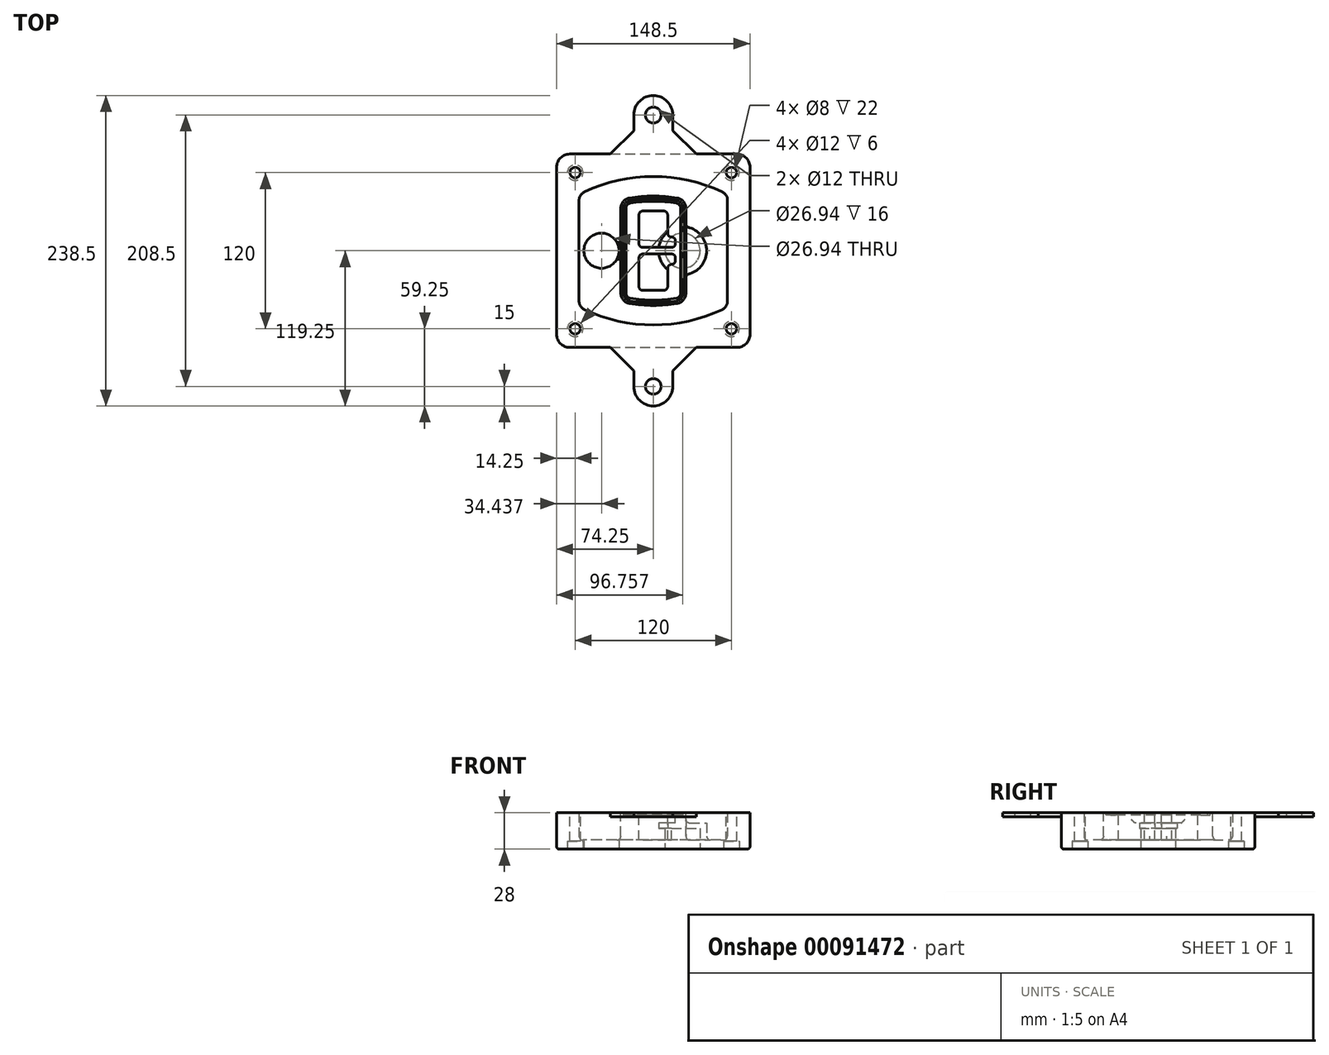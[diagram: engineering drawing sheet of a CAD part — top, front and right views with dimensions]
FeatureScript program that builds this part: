
annotation { "Feature Type Name" : "Feature", "Feature Type Description" : "" }
export const myFeature = defineFeature(function(context is Context, id is Id, definition is map)
    precondition{}
    {
        {
            var Q0;
            Q0=qCreatedBy(makeId("Top.planeOp"),FACE);
            var sketch = newSketch(context, id + "F0", { "sketchPlane" : qUnion([Q0])});
            skPoint(sketch, "E0.rect.middle", {"position": v(0, 0) * mm});
            skLineSegment(sketch, "E1.bottom", {"start": v(-64.25, -74.25) * mm, "end": v(64.25, -74.25) * mm});
            skLineSegment(sketch, "E1.top", {"start": v(-64.25, 74.25) * mm, "end": v(64.25, 74.25) * mm});
            skLineSegment(sketch, "E1.left", {"start": v(-74.25, -64.25) * mm, "end": v(-74.25, 64.25) * mm});
            skLineSegment(sketch, "E1.right", {"start": v(74.25, -64.25) * mm, "end": v(74.25, 64.25) * mm});
            skLineSegment(sketch, "E2", {"start": v(-74.25, 74.25) * mm, "end": v(74.25, -74.25) * mm, "construction": true});
            skLineSegment(sketch, "E3", {"start": v(74.25, 74.25) * mm, "end": v(-74.25, -74.25) * mm, "construction": true});
            skCircle(sketch, "E4", {"center": v(-60, 60) * mm, "radius": 4 * mm});
            skCircle(sketch, "E5", {"center": v(60, 60) * mm, "radius": 4 * mm});
            skCircle(sketch, "E6", {"center": v(60, -60) * mm, "radius": 4 * mm});
            skCircle(sketch, "E7", {"center": v(-60, -60) * mm, "radius": 4 * mm});
            skLineSegment(sketch, "E8", {"start": v(-60, 60) * mm, "end": v(60, 60) * mm, "construction": true});
            skLineSegment(sketch, "E9", {"start": v(60, 60) * mm, "end": v(60, -60) * mm, "construction": true});
            skLineSegment(sketch, "E10", {"start": v(60, -60) * mm, "end": v(-60, -60) * mm, "construction": true});
            skLineSegment(sketch, "E11", {"start": v(-60, -60) * mm, "end": v(-60, 60) * mm, "construction": true});
            skLineSegment(sketch, "E12", {"start": v(-60, 38.83) * mm, "end": v(-60, -38.83) * mm});
            skLineSegment(sketch, "E13", {"start": v(60, 38.83) * mm, "end": v(60, -38.83) * mm});
            skArc(sketch, "E14", {"start": v(54.26, 47.88) * mm, "mid": v(0, 60) * mm, "end": v(-54.26, 47.88) * mm});
            skArc(sketch, "E15", {"start": v(-54.26, -47.88) * mm, "mid": v(0, -60) * mm, "end": v(54.26, -47.88) * mm});
            skLineSegment(sketch, "E16", {"start": v(-60, 0) * mm, "end": v(60, 0) * mm, "construction": true});
            skPoint(sketch, "E17.visualSharp", {"position": v(-60, -45) * mm});
            skArc(sketch, "E17.filletArc", {"start": v(-60, -38.83) * mm, "mid": v(-58.44, -44.2) * mm, "end": v(-54.26, -47.88) * mm});
            skPoint(sketch, "E18.visualSharp", {"position": v(-60, 45) * mm});
            skArc(sketch, "E18.filletArc", {"start": v(-54.26, 47.88) * mm, "mid": v(-58.44, 44.2) * mm, "end": v(-60, 38.83) * mm});
            skPoint(sketch, "E19.visualSharp", {"position": v(60, 45) * mm});
            skArc(sketch, "E19.filletArc", {"start": v(60, 38.83) * mm, "mid": v(58.44, 44.2) * mm, "end": v(54.26, 47.88) * mm});
            skPoint(sketch, "E20.visualSharp", {"position": v(60, -45) * mm});
            skArc(sketch, "E20.filletArc", {"start": v(54.26, -47.88) * mm, "mid": v(58.44, -44.2) * mm, "end": v(60, -38.83) * mm});
            skPoint(sketch, "E21.visualSharp", {"position": v(-74.25, 74.25) * mm});
            skArc(sketch, "E21.filletArc", {"start": v(-64.25, 74.25) * mm, "mid": v(-71.32, 71.32) * mm, "end": v(-74.25, 64.25) * mm});
            skPoint(sketch, "E22.visualSharp", {"position": v(74.25, 74.25) * mm});
            skArc(sketch, "E22.filletArc", {"start": v(74.25, 64.25) * mm, "mid": v(71.32, 71.32) * mm, "end": v(64.25, 74.25) * mm});
            skPoint(sketch, "E23.visualSharp", {"position": v(74.25, -74.25) * mm});
            skArc(sketch, "E23.filletArc", {"start": v(64.25, -74.25) * mm, "mid": v(71.32, -71.32) * mm, "end": v(74.25, -64.25) * mm});
            skPoint(sketch, "E24.visualSharp", {"position": v(-74.25, -74.25) * mm});
            skArc(sketch, "E24.filletArc", {"start": v(-74.25, -64.25) * mm, "mid": v(-71.32, -71.32) * mm, "end": v(-64.25, -74.25) * mm});
            skArc(sketch, "E25.0", {"start": v(57, 38.83) * mm, "mid": v(55.9, 42.58) * mm, "end": v(52.98, 45.17) * mm});
            skLineSegment(sketch, "E25.1", {"start": v(57, 38.83) * mm, "end": v(57, -38.83) * mm});
            skArc(sketch, "E25.2", {"start": v(52.98, -45.17) * mm, "mid": v(55.9, -42.58) * mm, "end": v(57, -38.83) * mm});
            skArc(sketch, "E25.3", {"start": v(-52.98, -45.17) * mm, "mid": v(0, -57) * mm, "end": v(52.98, -45.17) * mm});
            skArc(sketch, "E25.4", {"start": v(-57, -38.83) * mm, "mid": v(-55.9, -42.58) * mm, "end": v(-52.98, -45.17) * mm});
            skArc(sketch, "E25.5", {"start": v(52.98, 45.17) * mm, "mid": v(0, 57) * mm, "end": v(-52.98, 45.17) * mm});
            skLineSegment(sketch, "E25.6", {"start": v(-57, 38.83) * mm, "end": v(-57, -38.83) * mm});
            skArc(sketch, "E25.7", {"start": v(-52.98, 45.17) * mm, "mid": v(-55.9, 42.58) * mm, "end": v(-57, 38.83) * mm});
            skArc(sketch, "E26.0", {"start": v(-55.96, 51.5) * mm, "mid": v(-61.82, 46.33) * mm, "end": v(-64, 38.83) * mm});
            skArc(sketch, "E26.1", {"start": v(55.96, 51.5) * mm, "mid": v(0, 64) * mm, "end": v(-55.96, 51.5) * mm});
            skArc(sketch, "E26.2", {"start": v(64, 38.83) * mm, "mid": v(61.82, 46.33) * mm, "end": v(55.96, 51.5) * mm});
            skLineSegment(sketch, "E26.3", {"start": v(64, 38.83) * mm, "end": v(64, -38.83) * mm});
            skArc(sketch, "E26.4", {"start": v(55.96, -51.5) * mm, "mid": v(61.82, -46.33) * mm, "end": v(64, -38.83) * mm});
            skLineSegment(sketch, "E26.5", {"start": v(-64, 38.83) * mm, "end": v(-64, -38.83) * mm});
            skArc(sketch, "E26.6", {"start": v(-55.96, -51.5) * mm, "mid": v(0, -64) * mm, "end": v(55.96, -51.5) * mm});
            skArc(sketch, "E26.7", {"start": v(-64, -38.83) * mm, "mid": v(-61.82, -46.33) * mm, "end": v(-55.96, -51.5) * mm});
            skSolve(sketch);
        }
        {
            var Q0;
            Q0=makeQuery(id+"F0.imprint","IMPRINT",FACE,{"disambiguationData":[TD([[makeQuery(id+"F0.imprint","IMPRINT",EDGE,{"derivedFrom":sQuery(id+"F0.wireOp",EDGE,"E1.bottom")}),1.0]])]});
            var Q1;
            Q1=makeQuery(id+"F0.imprint","IMPRINT",FACE,{"disambiguationData":[TD([[makeQuery(id+"F0.imprint","IMPRINT",EDGE,{"derivedFrom":sQuery(id+"F0.wireOp",EDGE,"E12")}),1.0]])]});
            var Q2;
            Q2=makeQuery(id+"F0.imprint","IMPRINT",FACE,{"disambiguationData":[TD([[makeQuery(id+"F0.imprint","IMPRINT",EDGE,{"derivedFrom":sQuery(id+"F0.wireOp",EDGE,"E25.0")}),1.0]])]});
            var Q3;
            Q3=makeQuery(id+"F0.imprint","IMPRINT",FACE,{"disambiguationData":[TD([[makeQuery(id+"F0.imprint","IMPRINT",EDGE,{"derivedFrom":sQuery(id+"F0.wireOp",EDGE,"E12")}),-1.0]])]});
            extrude(context, id + "F1", {"entities" : qUnion([Q0, Q1, Q2, Q3]), "oppositeDirection" : true, "depth" : 25 * mm});
        }
        {
            var Q0;
            Q0=makeQuery(id+"F0.imprint","IMPRINT",FACE,{"disambiguationData":[TD([[makeQuery(id+"F0.imprint","IMPRINT",EDGE,{"derivedFrom":sQuery(id+"F0.wireOp",EDGE,"E12")}),1.0]])]});
            extrude(context, id + "F2", {"entities" : qUnion([Q0]), "operationType" : NewBodyOperationType.ADD, "depth" : 3 * mm});
        }
        {
            var Q0;
            Q0=makeQuery(id+"F0.imprint","IMPRINT",FACE,{"disambiguationData":[TD([[makeQuery(id+"F0.imprint","IMPRINT",EDGE,{"derivedFrom":sQuery(id+"F0.wireOp",EDGE,"E25.0")}),1.0]])]});
            extrude(context, id + "F3", {"entities" : qUnion([Q0]), "operationType" : NewBodyOperationType.REMOVE, "oppositeDirection" : true, "depth" : 18 * mm});
        }
        {
            var Q0;
            Q0=makeQuery(id+"F2.opExtrude","CAP_FACE",FACE,{"disambiguationData":[OSD([sQuery(id+"F0.wireOp",EDGE,"E12"),sQuery(id+"F0.wireOp",EDGE,"E13"),sQuery(id+"F0.wireOp",EDGE,"E14"),sQuery(id+"F0.wireOp",EDGE,"E15"),sQuery(id+"F0.wireOp",EDGE,"E17.filletArc"),sQuery(id+"F0.wireOp",EDGE,"E18.filletArc"),sQuery(id+"F0.wireOp",EDGE,"E19.filletArc"),sQuery(id+"F0.wireOp",EDGE,"E20.filletArc"),sQuery(id+"F0.wireOp",EDGE,"E25.0"),sQuery(id+"F0.wireOp",EDGE,"E25.1"),sQuery(id+"F0.wireOp",EDGE,"E25.2"),sQuery(id+"F0.wireOp",EDGE,"E25.3"),sQuery(id+"F0.wireOp",EDGE,"E25.4"),sQuery(id+"F0.wireOp",EDGE,"E25.5"),sQuery(id+"F0.wireOp",EDGE,"E25.6"),sQuery(id+"F0.wireOp",EDGE,"E25.7")])],"isStart":false});
            var sketch = newSketch(context, id + "F4", { "sketchPlane" : qUnion([Q0])});
            skArc(sketch, "E27.0", {"start": v(-18.34, -40.45) * mm, "mid": v(0, -42) * mm, "end": v(18.34, -40.45) * mm});
            skArc(sketch, "E28.0", {"start": v(18.34, 40.45) * mm, "mid": v(0, 42) * mm, "end": v(-18.34, 40.45) * mm});
            skLineSegment(sketch, "E29", {"start": v(-25, 32.57) * mm, "end": v(-25, -32.57) * mm});
            skLineSegment(sketch, "E30", {"start": v(25, 32.57) * mm, "end": v(25, -32.57) * mm});
            skLineSegment(sketch, "E31", {"start": v(-25, 39.1) * mm, "end": v(25, 39.1) * mm, "construction": true});
            skLineSegment(sketch, "E32", {"start": v(-25, -39.1) * mm, "end": v(25, -39.1) * mm, "construction": true});
            skPoint(sketch, "E33.visualSharp", {"position": v(-25, 39.1) * mm});
            skArc(sketch, "E33.filletArc", {"start": v(-18.34, 40.45) * mm, "mid": v(-23.11, 37.73) * mm, "end": v(-25, 32.57) * mm});
            skPoint(sketch, "E34.visualSharp", {"position": v(25, 39.1) * mm});
            skArc(sketch, "E34.filletArc", {"start": v(25, 32.57) * mm, "mid": v(23.11, 37.73) * mm, "end": v(18.34, 40.45) * mm});
            skPoint(sketch, "E35.visualSharp", {"position": v(25, -39.1) * mm});
            skArc(sketch, "E35.filletArc", {"start": v(18.34, -40.45) * mm, "mid": v(23.11, -37.73) * mm, "end": v(25, -32.57) * mm});
            skPoint(sketch, "E36.visualSharp", {"position": v(-25, -39.1) * mm});
            skArc(sketch, "E36.filletArc", {"start": v(-25, -32.57) * mm, "mid": v(-23.11, -37.73) * mm, "end": v(-18.34, -40.45) * mm});
            skArc(sketch, "E37.0", {"start": v(52.98, 45.17) * mm, "mid": v(0, 57) * mm, "end": v(-52.98, 45.17) * mm});
            skArc(sketch, "E37.1", {"start": v(-52.98, 45.17) * mm, "mid": v(-55.9, 42.58) * mm, "end": v(-57, 38.83) * mm});
            skLineSegment(sketch, "E37.2", {"start": v(-57, 38.83) * mm, "end": v(-57, -38.83) * mm});
            skArc(sketch, "E37.3", {"start": v(-57, -38.83) * mm, "mid": v(-55.9, -42.58) * mm, "end": v(-52.98, -45.17) * mm});
            skArc(sketch, "E37.4", {"start": v(-52.98, -45.17) * mm, "mid": v(0, -57) * mm, "end": v(52.98, -45.17) * mm});
            skArc(sketch, "E37.5", {"start": v(52.98, -45.17) * mm, "mid": v(55.9, -42.58) * mm, "end": v(57, -38.83) * mm});
            skLineSegment(sketch, "E37.6", {"start": v(57, 38.83) * mm, "end": v(57, -38.83) * mm});
            skArc(sketch, "E37.7", {"start": v(57, 38.83) * mm, "mid": v(55.9, 42.58) * mm, "end": v(52.98, 45.17) * mm});
            skLineSegment(sketch, "E38.0", {"start": v(23, 32.57) * mm, "end": v(23, -32.57) * mm});
            skArc(sketch, "E38.1", {"start": v(18, -38.48) * mm, "mid": v(21.58, -36.44) * mm, "end": v(23, -32.57) * mm});
            skArc(sketch, "E38.2", {"start": v(-18, -38.48) * mm, "mid": v(0, -40) * mm, "end": v(18, -38.48) * mm});
            skArc(sketch, "E38.3", {"start": v(-23, -32.57) * mm, "mid": v(-21.58, -36.44) * mm, "end": v(-18, -38.48) * mm});
            skLineSegment(sketch, "E38.4", {"start": v(-23, 32.57) * mm, "end": v(-23, -32.57) * mm});
            skArc(sketch, "E38.5", {"start": v(23, 32.57) * mm, "mid": v(21.58, 36.44) * mm, "end": v(18, 38.48) * mm});
            skArc(sketch, "E38.6", {"start": v(-18, 38.48) * mm, "mid": v(-21.58, 36.44) * mm, "end": v(-23, 32.57) * mm});
            skArc(sketch, "E38.7", {"start": v(18, 38.48) * mm, "mid": v(0, 40) * mm, "end": v(-18, 38.48) * mm});
            skArc(sketch, "E39.0", {"start": v(21, 32.57) * mm, "mid": v(20.06, 35.15) * mm, "end": v(17.67, 36.5) * mm});
            skLineSegment(sketch, "E39.1", {"start": v(21, 32.57) * mm, "end": v(21, -32.57) * mm});
            skArc(sketch, "E39.2", {"start": v(17.67, -36.5) * mm, "mid": v(20.06, -35.15) * mm, "end": v(21, -32.57) * mm});
            skArc(sketch, "E39.3", {"start": v(-17.67, -36.5) * mm, "mid": v(0, -38) * mm, "end": v(17.67, -36.5) * mm});
            skArc(sketch, "E39.4", {"start": v(-21, -32.57) * mm, "mid": v(-20.06, -35.15) * mm, "end": v(-17.67, -36.5) * mm});
            skArc(sketch, "E39.5", {"start": v(17.67, 36.5) * mm, "mid": v(0, 38) * mm, "end": v(-17.67, 36.5) * mm});
            skLineSegment(sketch, "E39.6", {"start": v(-21, 32.57) * mm, "end": v(-21, -32.57) * mm});
            skArc(sketch, "E39.7", {"start": v(-17.67, 36.5) * mm, "mid": v(-20.06, 35.15) * mm, "end": v(-21, 32.57) * mm});
            skLineSegment(sketch, "E40", {"start": v(-25, 0) * mm, "end": v(25, 0) * mm, "construction": true});
            skLineSegment(sketch, "E41", {"start": v(-11, 5.5) * mm, "end": v(-11, 27.5) * mm});
            skLineSegment(sketch, "E42", {"start": v(-8, 30.5) * mm, "end": v(8, 30.5) * mm});
            skLineSegment(sketch, "E43", {"start": v(11, 27.5) * mm, "end": v(11, 13.5) * mm});
            skLineSegment(sketch, "E44", {"start": v(14, 10.5) * mm, "end": v(14, 10.5) * mm});
            skLineSegment(sketch, "E45", {"start": v(17, 7.5) * mm, "end": v(17, 5.5) * mm});
            skLineSegment(sketch, "E46", {"start": v(14, 2.5) * mm, "end": v(-8, 2.5) * mm});
            skPoint(sketch, "E47.visualSharp", {"position": v(-11, 30.5) * mm});
            skArc(sketch, "E47.filletArc", {"start": v(-8, 30.5) * mm, "mid": v(-10.12, 29.62) * mm, "end": v(-11, 27.5) * mm});
            skPoint(sketch, "E48.visualSharp", {"position": v(11, 30.5) * mm});
            skArc(sketch, "E48.filletArc", {"start": v(11, 27.5) * mm, "mid": v(10.12, 29.62) * mm, "end": v(8, 30.5) * mm});
            skPoint(sketch, "E49.visualSharp", {"position": v(11, 10.5) * mm});
            skArc(sketch, "E49.filletArc", {"start": v(11, 13.5) * mm, "mid": v(11.88, 11.38) * mm, "end": v(14, 10.5) * mm});
            skPoint(sketch, "E50.visualSharp", {"position": v(17, 10.5) * mm});
            skArc(sketch, "E50.filletArc", {"start": v(17, 7.5) * mm, "mid": v(16.12, 9.62) * mm, "end": v(14, 10.5) * mm});
            skPoint(sketch, "E51.visualSharp", {"position": v(17, 2.5) * mm});
            skArc(sketch, "E51.filletArc", {"start": v(14, 2.5) * mm, "mid": v(16.12, 3.38) * mm, "end": v(17, 5.5) * mm});
            skPoint(sketch, "E52.visualSharp", {"position": v(-11, 2.5) * mm});
            skArc(sketch, "E52.filletArc", {"start": v(-11, 5.5) * mm, "mid": v(-10.12, 3.38) * mm, "end": v(-8, 2.5) * mm});
            skLineSegment(sketch, "E53.0.MirrorCS", {"start": v(14, -2.5) * mm, "end": v(-8, -2.5) * mm});
            skArc(sketch, "E54.0.MirrorCS", {"start": v(-11, -5.5) * mm, "mid": v(-10.12, -3.38) * mm, "end": v(-8, -2.5) * mm});
            skLineSegment(sketch, "E55.0.MirrorCS", {"start": v(-11, -5.5) * mm, "end": v(-11, -27.5) * mm});
            skArc(sketch, "E56.0.MirrorCS", {"start": v(-8, -30.5) * mm, "mid": v(-10.12, -29.62) * mm, "end": v(-11, -27.5) * mm});
            skLineSegment(sketch, "E57.0.MirrorCS", {"start": v(-8, -30.5) * mm, "end": v(8, -30.5) * mm});
            skArc(sketch, "E58.0.MirrorCS", {"start": v(11, -27.5) * mm, "mid": v(10.12, -29.62) * mm, "end": v(8, -30.5) * mm});
            skLineSegment(sketch, "E59.0.MirrorCS", {"start": v(11, -27.5) * mm, "end": v(11, -13.5) * mm});
            skArc(sketch, "E60.0.MirrorCS", {"start": v(11, -13.5) * mm, "mid": v(11.88, -11.38) * mm, "end": v(14, -10.5) * mm});
            skArc(sketch, "E61.0.MirrorCS", {"start": v(17, -7.5) * mm, "mid": v(16.12, -9.62) * mm, "end": v(14, -10.5) * mm});
            skLineSegment(sketch, "E62.0.MirrorCS", {"start": v(17, -7.5) * mm, "end": v(17, -5.5) * mm});
            skArc(sketch, "E63.0.MirrorCS", {"start": v(14, -2.5) * mm, "mid": v(16.12, -3.38) * mm, "end": v(17, -5.5) * mm});
            skSolve(sketch);
        }
        {
            var Q0;
            Q0=makeQuery(id+"F4.imprint","IMPRINT",FACE,{"disambiguationData":[TD([[makeQuery(id+"F4.imprint","IMPRINT",EDGE,{"derivedFrom":sQuery(id+"F4.wireOp",EDGE,"E27.0")}),1.0]])]});
            var Q1;
            Q1=makeQuery(id+"F4.imprint","IMPRINT",FACE,{"disambiguationData":[TD([[makeQuery(id+"F4.imprint","IMPRINT",EDGE,{"derivedFrom":sQuery(id+"F4.wireOp",EDGE,"E38.0")}),-1.0]])]});
            var Q2;
            Q2=makeQuery(id+"F4.imprint","IMPRINT",FACE,{"disambiguationData":[TD([[makeQuery(id+"F4.imprint","IMPRINT",EDGE,{"derivedFrom":sQuery(id+"F4.wireOp",EDGE,"E39.0")}),1.0]])]});
            extrude(context, id + "F5", {"entities" : qUnion([Q0, Q1, Q2]), "operationType" : NewBodyOperationType.ADD, "endBound" : BoundingType.UP_TO_NEXT, "oppositeDirection" : true, "depth" : 25 * mm});
        }
        {
            var Q0;
            Q0=makeQuery(id+"F4.imprint","IMPRINT",FACE,{"disambiguationData":[TD([[makeQuery(id+"F4.imprint","IMPRINT",EDGE,{"derivedFrom":sQuery(id+"F4.wireOp",EDGE,"E38.0")}),-1.0]])]});
            extrude(context, id + "F6", {"entities" : qUnion([Q0]), "operationType" : NewBodyOperationType.REMOVE, "oppositeDirection" : true, "depth" : 2 * mm});
        }
        {
            var Q0;
            Q0=makeQuery(id+"F1.opExtrude","CAP_FACE",FACE,{"disambiguationData":[OSD([sQuery(id+"F0.wireOp",EDGE,"E1.bottom"),sQuery(id+"F0.wireOp",EDGE,"E1.top"),sQuery(id+"F0.wireOp",EDGE,"E1.left"),sQuery(id+"F0.wireOp",EDGE,"E1.right"),sQuery(id+"F0.wireOp",EDGE,"E4"),sQuery(id+"F0.wireOp",EDGE,"E5"),sQuery(id+"F0.wireOp",EDGE,"E6"),sQuery(id+"F0.wireOp",EDGE,"E7"),sQuery(id+"F0.wireOp",EDGE,"E21.filletArc"),sQuery(id+"F0.wireOp",EDGE,"E22.filletArc"),sQuery(id+"F0.wireOp",EDGE,"E23.filletArc"),sQuery(id+"F0.wireOp",EDGE,"E24.filletArc")])],"isStart":false});
            var sketch = newSketch(context, id + "F7", { "sketchPlane" : qUnion([Q0])});
            skCircle(sketch, "E64", {"center": v(22.5, 0) * mm, "radius": 13.47 * mm});
            skCircle(sketch, "E65", {"center": v(-39.81, 0) * mm, "radius": 13.47 * mm});
            skLineSegment(sketch, "E66", {"start": v(74.25, 0) * mm, "end": v(-74.25, 0) * mm});
            skCircle(sketch, "E67", {"center": v(22.5, 0) * mm, "radius": 18.47 * mm});
            skCircle(sketch, "E68", {"center": v(60, -60) * mm, "radius": 6 * mm});
            skCircle(sketch, "E69", {"center": v(-60, -60) * mm, "radius": 6 * mm});
            skCircle(sketch, "E70", {"center": v(-60, 60) * mm, "radius": 6 * mm});
            skCircle(sketch, "E71", {"center": v(60, 60) * mm, "radius": 6 * mm});
            skSolve(sketch);
        }
        {
            var Q0;
            {var subQ1=sQuery(id+"F7.wireOp",EDGE,"E66");var subQ4=sQuery(id+"F7.wireOp",EDGE,"E64");var subQ6=makeQuery(id+"F7.imprint","INTERSECT",VERTEX,{"disambiguationData":[OD(0.0)],"derivedFrom":[subQ4,subQ1]});Q0=makeQuery(id+"F7.imprint","IMPRINT",FACE,{"disambiguationData":[TD([[makeQuery(id+"F7.imprint","IMPRINT",EDGE,{"disambiguationData":[TD([[subQ6,-1.0]])],"derivedFrom":subQ4}),-1.0]])]});}
            var Q1;
            {var subQ0=sQuery(id+"F7.wireOp",EDGE,"E66");var subQ1=sQuery(id+"F7.wireOp",EDGE,"E64");var subQ3=makeQuery(id+"F7.imprint","INTERSECT",VERTEX,{"disambiguationData":[OD(0.0)],"derivedFrom":[subQ1,subQ0]});Q1=makeQuery(id+"F7.imprint","IMPRINT",FACE,{"disambiguationData":[TD([[makeQuery(id+"F7.imprint","IMPRINT",EDGE,{"disambiguationData":[TD([[subQ3,-1.0]])],"derivedFrom":subQ1}),1.0]])]});}
            var Q2;
            {var subQ0=sQuery(id+"F7.wireOp",EDGE,"E66");var subQ1=sQuery(id+"F7.wireOp",EDGE,"E64");var subQ3=makeQuery(id+"F7.imprint","INTERSECT",VERTEX,{"disambiguationData":[OD(0.0)],"derivedFrom":[subQ1,subQ0]});Q2=makeQuery(id+"F7.imprint","IMPRINT",FACE,{"disambiguationData":[TD([[makeQuery(id+"F7.imprint","IMPRINT",EDGE,{"disambiguationData":[TD([[subQ3,1.0]])],"derivedFrom":subQ1}),1.0]])]});}
            var Q3;
            {var subQ1=sQuery(id+"F7.wireOp",EDGE,"E66");var subQ4=sQuery(id+"F7.wireOp",EDGE,"E64");var subQ6=makeQuery(id+"F7.imprint","INTERSECT",VERTEX,{"disambiguationData":[OD(0.0)],"derivedFrom":[subQ4,subQ1]});Q3=makeQuery(id+"F7.imprint","IMPRINT",FACE,{"disambiguationData":[TD([[makeQuery(id+"F7.imprint","IMPRINT",EDGE,{"disambiguationData":[TD([[subQ6,1.0]])],"derivedFrom":subQ4}),-1.0]])]});}
            extrude(context, id + "F8", {"entities" : qUnion([Q0, Q1, Q2, Q3]), "operationType" : NewBodyOperationType.ADD, "oppositeDirection" : true, "depth" : 20 * mm});
        }
        {
            var Q0;
            {var subQ0=sQuery(id+"F7.wireOp",EDGE,"E66");var subQ1=sQuery(id+"F7.wireOp",EDGE,"E64");var subQ3=makeQuery(id+"F7.imprint","INTERSECT",VERTEX,{"disambiguationData":[OD(0.0)],"derivedFrom":[subQ1,subQ0]});Q0=makeQuery(id+"F7.imprint","IMPRINT",FACE,{"disambiguationData":[TD([[makeQuery(id+"F7.imprint","IMPRINT",EDGE,{"disambiguationData":[TD([[subQ3,-1.0]])],"derivedFrom":subQ1}),1.0]])]});}
            var Q1;
            {var subQ0=sQuery(id+"F7.wireOp",EDGE,"E66");var subQ1=sQuery(id+"F7.wireOp",EDGE,"E64");var subQ3=makeQuery(id+"F7.imprint","INTERSECT",VERTEX,{"disambiguationData":[OD(0.0)],"derivedFrom":[subQ1,subQ0]});Q1=makeQuery(id+"F7.imprint","IMPRINT",FACE,{"disambiguationData":[TD([[makeQuery(id+"F7.imprint","IMPRINT",EDGE,{"disambiguationData":[TD([[subQ3,1.0]])],"derivedFrom":subQ1}),1.0]])]});}
            extrude(context, id + "F9", {"entities" : qUnion([Q0, Q1]), "operationType" : NewBodyOperationType.REMOVE, "oppositeDirection" : true, "depth" : 16 * mm});
        }
        {
            var Q0;
            {var subQ0=sQuery(id+"F7.wireOp",EDGE,"E66");var subQ1=sQuery(id+"F7.wireOp",EDGE,"E65");var subQ3=makeQuery(id+"F7.imprint","INTERSECT",VERTEX,{"disambiguationData":[OD(0.0)],"derivedFrom":[subQ1,subQ0]});Q0=makeQuery(id+"F7.imprint","IMPRINT",FACE,{"disambiguationData":[TD([[makeQuery(id+"F7.imprint","IMPRINT",EDGE,{"disambiguationData":[TD([[subQ3,-1.0]])],"derivedFrom":subQ1}),1.0]])]});}
            var Q1;
            {var subQ0=sQuery(id+"F7.wireOp",EDGE,"E66");var subQ1=sQuery(id+"F7.wireOp",EDGE,"E65");var subQ3=makeQuery(id+"F7.imprint","INTERSECT",VERTEX,{"disambiguationData":[OD(0.0)],"derivedFrom":[subQ1,subQ0]});Q1=makeQuery(id+"F7.imprint","IMPRINT",FACE,{"disambiguationData":[TD([[makeQuery(id+"F7.imprint","IMPRINT",EDGE,{"disambiguationData":[TD([[subQ3,1.0]])],"derivedFrom":subQ1}),1.0]])]});}
            extrude(context, id + "F10", {"entities" : qUnion([Q0, Q1]), "operationType" : NewBodyOperationType.REMOVE, "oppositeDirection" : true, "depth" : 25 * mm});
        }
        {
            var Q0;
            Q0=makeQuery(id+"F7.imprint","IMPRINT",FACE,{"disambiguationData":[TD([[makeQuery(id+"F7.imprint","IMPRINT",EDGE,{"derivedFrom":sQuery(id+"F7.wireOp",EDGE,"E68")}),1.0]])]});
            var Q1;
            Q1=makeQuery(id+"F7.imprint","IMPRINT",FACE,{"disambiguationData":[TD([[makeQuery(id+"F7.imprint","IMPRINT",EDGE,{"derivedFrom":makeQuery(id+"F1.opExtrude","CAP_EDGE",EDGE,{"disambiguationData":[OSD([sQuery(id+"F0.wireOp",EDGE,"E5")])],"isStart":false})}),-1.0]])]});
            var Q2;
            Q2=makeQuery(id+"F7.imprint","IMPRINT",FACE,{"disambiguationData":[TD([[makeQuery(id+"F7.imprint","IMPRINT",EDGE,{"derivedFrom":sQuery(id+"F7.wireOp",EDGE,"E69")}),1.0]])]});
            var Q3;
            Q3=makeQuery(id+"F7.imprint","IMPRINT",FACE,{"disambiguationData":[TD([[makeQuery(id+"F7.imprint","IMPRINT",EDGE,{"derivedFrom":makeQuery(id+"F1.opExtrude","CAP_EDGE",EDGE,{"disambiguationData":[OSD([sQuery(id+"F0.wireOp",EDGE,"E4")])],"isStart":false})}),-1.0]])]});
            var Q4;
            Q4=makeQuery(id+"F7.imprint","IMPRINT",FACE,{"disambiguationData":[TD([[makeQuery(id+"F7.imprint","IMPRINT",EDGE,{"derivedFrom":sQuery(id+"F7.wireOp",EDGE,"E70")}),1.0]])]});
            var Q5;
            Q5=makeQuery(id+"F7.imprint","IMPRINT",FACE,{"disambiguationData":[TD([[makeQuery(id+"F7.imprint","IMPRINT",EDGE,{"derivedFrom":makeQuery(id+"F1.opExtrude","CAP_EDGE",EDGE,{"disambiguationData":[OSD([sQuery(id+"F0.wireOp",EDGE,"E7")])],"isStart":false})}),-1.0]])]});
            var Q6;
            Q6=makeQuery(id+"F7.imprint","IMPRINT",FACE,{"disambiguationData":[TD([[makeQuery(id+"F7.imprint","IMPRINT",EDGE,{"derivedFrom":sQuery(id+"F7.wireOp",EDGE,"E71")}),1.0]])]});
            var Q7;
            Q7=makeQuery(id+"F7.imprint","IMPRINT",FACE,{"disambiguationData":[TD([[makeQuery(id+"F7.imprint","IMPRINT",EDGE,{"derivedFrom":makeQuery(id+"F1.opExtrude","CAP_EDGE",EDGE,{"disambiguationData":[OSD([sQuery(id+"F0.wireOp",EDGE,"E6")])],"isStart":false})}),-1.0]])]});
            extrude(context, id + "F11", {"entities" : qUnion([Q0, Q1, Q2, Q3, Q4, Q5, Q6, Q7]), "operationType" : NewBodyOperationType.REMOVE, "oppositeDirection" : true, "depth" : 6 * mm});
        }
        {
            var Q0;
            Q0=makeQuery(id+"F9.boolean.opBoolean","COPY",FACE,{"derivedFrom":makeQuery(id+"F9.opExtrude","CAP_FACE",FACE,{"disambiguationData":[OSD([sQuery(id+"F7.wireOp",EDGE,"E64")])],"isStart":false})});
            var sketch = newSketch(context, id + "F12", { "sketchPlane" : qUnion([Q0])});
            skArc(sketch, "E72.0", {"start": v(11, 14.45) * mm, "mid": v(6.45, 9.13) * mm, "end": v(4.2, 2.5) * mm});
            skArc(sketch, "E72.1", {"start": v(4.2, -2.5) * mm, "mid": v(6.45, -9.13) * mm, "end": v(11, -14.45) * mm});
            skLineSegment(sketch, "E73", {"start": v(4.2, -2.5) * mm, "end": v(14, -2.5) * mm});
            skLineSegment(sketch, "E74.0", {"start": v(14, 2.5) * mm, "end": v(4.2, 2.5) * mm});
            skArc(sketch, "E74.1", {"start": v(14, 2.5) * mm, "mid": v(16.12, 3.38) * mm, "end": v(17, 5.5) * mm});
            skLineSegment(sketch, "E74.2", {"start": v(17, 7.5) * mm, "end": v(17, 5.5) * mm});
            skArc(sketch, "E74.3", {"start": v(17, 7.5) * mm, "mid": v(16.12, 9.62) * mm, "end": v(14, 10.5) * mm});
            skArc(sketch, "E74.4", {"start": v(11, 13.5) * mm, "mid": v(11.88, 11.38) * mm, "end": v(14, 10.5) * mm});
            skLineSegment(sketch, "E74.5", {"start": v(11, 14.45) * mm, "end": v(11, 13.5) * mm});
            skLineSegment(sketch, "E74.7", {"start": v(14, -2.5) * mm, "end": v(4.2, -2.5) * mm});
            skArc(sketch, "E74.8", {"start": v(14, -2.5) * mm, "mid": v(16.12, -3.38) * mm, "end": v(17, -5.5) * mm});
            skLineSegment(sketch, "E74.9", {"start": v(17, -7.5) * mm, "end": v(17, -5.5) * mm});
            skArc(sketch, "E74.10", {"start": v(17, -7.5) * mm, "mid": v(16.12, -9.62) * mm, "end": v(14, -10.5) * mm});
            skArc(sketch, "E74.11", {"start": v(11, -13.5) * mm, "mid": v(11.88, -11.38) * mm, "end": v(14, -10.5) * mm});
            skLineSegment(sketch, "E74.12", {"start": v(11, -14.45) * mm, "end": v(11, -13.5) * mm});
            skPoint(sketch, "E75.orphan", {"position": v(11, -27.5) * mm});
            skPoint(sketch, "E76.orphan", {"position": v(-8, -2.5) * mm});
            skPoint(sketch, "E77.orphan", {"position": v(-8, 2.5) * mm});
            skPoint(sketch, "E78.orphan", {"position": v(11, 27.5) * mm});
            skSolve(sketch);
        }
        {
            var Q0;
            {var subQ7=sQuery(id+"F12.wireOp",EDGE,"E72.0");var subQ14=sQuery(id+"F12.wireOp",EDGE,"E72.1");var subQ16=sQuery(id+"F12.wireOp",EDGE,"E74.1");var subQ18=sQuery(id+"F12.wireOp",EDGE,"E74.8");Q0=qUnion([makeQuery(id+"F12.imprint","IMPRINT",FACE,{"disambiguationData":[TD([[makeQuery(id+"F12.imprint","IMPRINT",EDGE,{"derivedFrom":subQ7}),1.0]])]}),makeQuery(id+"F12.imprint","IMPRINT",FACE,{"disambiguationData":[TD([[makeQuery(id+"F12.imprint","IMPRINT",EDGE,{"derivedFrom":subQ14}),1.0]])]}),makeQuery(id+"F12.imprint","IMPRINT",FACE,{"disambiguationData":[TD([[makeQuery(id+"F12.imprint","IMPRINT",EDGE,{"derivedFrom":subQ16}),1.0]])]}),makeQuery(id+"F12.imprint","IMPRINT",FACE,{"disambiguationData":[TD([[makeQuery(id+"F12.imprint","IMPRINT",EDGE,{"derivedFrom":subQ18}),-1.0]])]})]);}
            var Q1;
            Q1=makeQuery(id+"F5.boolean.opBoolean","SPLIT",FACE,{"disambiguationData":[TD([makeQuery(id+"F5.opExtrude","SWEPT_FACE",FACE,{"disambiguationData":[OSD([sQuery(id+"F4.wireOp",EDGE,"E41")])]})])],"derivedFrom":makeQuery(id+"F3.boolean.opBoolean","COPY",FACE,{"derivedFrom":makeQuery(id+"F3.opExtrude","CAP_FACE",FACE,{"disambiguationData":[OSD([sQuery(id+"F0.wireOp",EDGE,"E25.0"),sQuery(id+"F0.wireOp",EDGE,"E25.1"),sQuery(id+"F0.wireOp",EDGE,"E25.2"),sQuery(id+"F0.wireOp",EDGE,"E25.3"),sQuery(id+"F0.wireOp",EDGE,"E25.4"),sQuery(id+"F0.wireOp",EDGE,"E25.5"),sQuery(id+"F0.wireOp",EDGE,"E25.6"),sQuery(id+"F0.wireOp",EDGE,"E25.7")])],"isStart":false})})});
            extrude(context, id + "F13", {"entities" : qUnion([Q0]), "operationType" : NewBodyOperationType.REMOVE, "endBound" : BoundingType.UP_TO_SURFACE, "endBoundEntityFace" : qUnion([Q1]), "depth" : 25 * mm});
        }
        {
            var Q0;
            Q0=makeQuery(id+"F3.boolean.opBoolean","COPY",EDGE,{"derivedFrom":makeQuery(id+"F3.opExtrude","CAP_EDGE",EDGE,{"disambiguationData":[OSD([sQuery(id+"F0.wireOp",EDGE,"E25.6")])],"isStart":false})});
            var Q1;
            Q1=makeQuery(id+"F8.boolean.opBoolean","INTERSECT",EDGE,{"derivedFrom":[makeQuery(id+"F5.opExtrude","SWEPT_FACE",FACE,{"disambiguationData":[OSD([sQuery(id+"F4.wireOp",EDGE,"E30")])]}),makeQuery(id+"F8.opExtrude","CAP_FACE",FACE,{"disambiguationData":[OSD([sQuery(id+"F7.wireOp",EDGE,"E67")])],"isStart":false})]});
            var Q2;
            Q2=makeQuery(id+"F8.boolean.opBoolean","INTERSECT",EDGE,{"disambiguationData":[OD(1.0)],"derivedFrom":[makeQuery(id+"F5.opExtrude","SWEPT_FACE",FACE,{"disambiguationData":[OSD([sQuery(id+"F4.wireOp",EDGE,"E30")])]}),makeQuery(id+"F8.opExtrude","SWEPT_FACE",FACE,{"disambiguationData":[OSD([sQuery(id+"F7.wireOp",EDGE,"E67")])]})]});
            var Q3;
            {var subQ0=sQuery(id+"F4.wireOp",EDGE,"E30");Q3=makeQuery(id+"F8.boolean.opBoolean","SPLIT",EDGE,{"disambiguationData":[TD([makeQuery(id+"F5.opExtrude","SWEPT_FACE",FACE,{"disambiguationData":[OSD([sQuery(id+"F4.wireOp",EDGE,"E35.filletArc")])]})])],"derivedFrom":makeQuery(id+"F5.opExtrude","CAP_EDGE",EDGE,{"disambiguationData":[OSD([subQ0])],"isStart":false})});}
            var Q4;
            {var subQ0=sQuery(id+"F0.wireOp",EDGE,"E25.7");var subQ1=sQuery(id+"F0.wireOp",EDGE,"E25.1");var subQ2=sQuery(id+"F0.wireOp",EDGE,"E25.6");var subQ3=sQuery(id+"F0.wireOp",EDGE,"E25.5");var subQ4=sQuery(id+"F0.wireOp",EDGE,"E25.4");var subQ5=sQuery(id+"F0.wireOp",EDGE,"E25.0");var subQ6=sQuery(id+"F0.wireOp",EDGE,"E25.2");var subQ7=sQuery(id+"F0.wireOp",EDGE,"E25.3");Q4=makeQuery(id+"F8.boolean.opBoolean","INTERSECT",EDGE,{"derivedFrom":[makeQuery(id+"F5.boolean.opBoolean","SPLIT",FACE,{"disambiguationData":[TD([makeQuery(id+"F2.opExtrude","SWEPT_FACE",FACE,{"disambiguationData":[OSD([subQ5])]})])],"derivedFrom":makeQuery(id+"F3.boolean.opBoolean","COPY",FACE,{"derivedFrom":makeQuery(id+"F3.opExtrude","CAP_FACE",FACE,{"disambiguationData":[OSD([subQ5,subQ1,subQ6,subQ7,subQ4,subQ3,subQ2,subQ0])],"isStart":false})})}),makeQuery(id+"F8.opExtrude","SWEPT_FACE",FACE,{"disambiguationData":[OSD([sQuery(id+"F7.wireOp",EDGE,"E67")])]})]});}
            var Q5;
            Q5=makeQuery(id+"F8.boolean.opBoolean","INTERSECT",EDGE,{"disambiguationData":[OD(0.0)],"derivedFrom":[makeQuery(id+"F5.opExtrude","SWEPT_FACE",FACE,{"disambiguationData":[OSD([sQuery(id+"F4.wireOp",EDGE,"E30")])]}),makeQuery(id+"F8.opExtrude","SWEPT_FACE",FACE,{"disambiguationData":[OSD([sQuery(id+"F7.wireOp",EDGE,"E67")])]})]});
            fillet(context, id + "F14", {"entities" : qUnion([Q0, Q1, Q2, Q3, Q4, Q5]), "radius" : 3 * mm, "tangentPropagation" : true, "allowEdgeOverflow" : false});
        }
        {
            var Q0;
            Q0=makeQuery(id+"F1.opExtrude","CAP_EDGE",EDGE,{"disambiguationData":[OSD([sQuery(id+"F0.wireOp",EDGE,"E1.bottom")])],"isStart":false});
            fillet(context, id + "F15", {"entities" : qUnion([Q0]), "radius" : 2 * mm, "tangentPropagation" : true, "allowEdgeOverflow" : false});
        }
        {
            var Q0;
            {var subQ0=sQuery(id+"F0.wireOp",EDGE,"E22.filletArc");var subQ1=sQuery(id+"F0.wireOp",EDGE,"E7");var subQ2=sQuery(id+"F0.wireOp",EDGE,"E6");var subQ3=sQuery(id+"F0.wireOp",EDGE,"E5");var subQ4=sQuery(id+"F0.wireOp",EDGE,"E4");var subQ5=sQuery(id+"F0.wireOp",EDGE,"E1.bottom");var subQ6=sQuery(id+"F0.wireOp",EDGE,"E21.filletArc");var subQ7=sQuery(id+"F0.wireOp",EDGE,"E1.top");var subQ8=sQuery(id+"F0.wireOp",EDGE,"E1.left");var subQ9=sQuery(id+"F0.wireOp",EDGE,"E1.right");var subQ10=sQuery(id+"F0.wireOp",EDGE,"E23.filletArc");var subQ11=sQuery(id+"F0.wireOp",EDGE,"E24.filletArc");Q0=makeQuery(id+"F2.boolean.opBoolean","SPLIT",FACE,{"disambiguationData":[TD([makeQuery(id+"F1.opExtrude","SWEPT_FACE",FACE,{"disambiguationData":[OSD([subQ5])]})])],"derivedFrom":makeQuery(id+"F1.opExtrude","CAP_FACE",FACE,{"disambiguationData":[OSD([subQ5,subQ7,subQ8,subQ9,subQ4,subQ3,subQ2,subQ1,subQ6,subQ0,subQ10,subQ11])],"isStart":true})});}
            var sketch = newSketch(context, id + "F16", { "sketchPlane" : qUnion([Q0])});
            skLineSegment(sketch, "E79", {"start": v(0, 74.25) * mm, "end": v(0, 104.25) * mm, "construction": true});
            skCircle(sketch, "E80", {"center": v(0, 104.25) * mm, "radius": 6 * mm});
            skLineSegment(sketch, "E81", {"start": v(-33, 74.25) * mm, "end": v(-15, 92.25) * mm});
            skLineSegment(sketch, "E82", {"start": v(-15, 92.25) * mm, "end": v(-15, 104.25) * mm});
            skLineSegment(sketch, "E83", {"start": v(33, 74.25) * mm, "end": v(15, 92.25) * mm});
            skLineSegment(sketch, "E84", {"start": v(15, 92.25) * mm, "end": v(15, 104.25) * mm});
            skArc(sketch, "E85", {"start": v(15, 104.25) * mm, "mid": v(0, 119.25) * mm, "end": v(-15, 104.25) * mm});
            skLineSegment(sketch, "E86", {"start": v(0, 0) * mm, "end": v(0, 104.25) * mm, "construction": true});
            skLineSegment(sketch, "E87.MirrorCS", {"start": v(-15, -92.25) * mm, "end": v(-15, -104.25) * mm});
            skCircle(sketch, "E88.MirrorC", {"center": v(0, -104.25) * mm, "radius": 6 * mm});
            skLineSegment(sketch, "E89.MirrorCS", {"start": v(15, -92.25) * mm, "end": v(15, -104.25) * mm});
            skArc(sketch, "E90.MirrorCS", {"start": v(15, -104.25) * mm, "mid": v(0, -119.25) * mm, "end": v(-15, -104.25) * mm});
            skLineSegment(sketch, "E91.MirrorCS", {"start": v(0, 0) * mm, "end": v(0, -104.25) * mm, "construction": true});
            skLineSegment(sketch, "E92.MirrorCS", {"start": v(0, -74.25) * mm, "end": v(0, -104.25) * mm, "construction": true});
            skLineSegment(sketch, "E93.MirrorCS", {"start": v(33, -74.25) * mm, "end": v(15, -92.25) * mm});
            skLineSegment(sketch, "E94.MirrorCS", {"start": v(-33, -74.25) * mm, "end": v(-15, -92.25) * mm});
            skSolve(sketch);
        }
        {
            var Q0;
            Q0=makeQuery(id+"F16.imprint","IMPRINT",FACE,{"disambiguationData":[TD([[makeQuery(id+"F16.imprint","IMPRINT",EDGE,{"derivedFrom":sQuery(id+"F16.wireOp",EDGE,"E87.MirrorCS")}),1.0]])]});
            var Q1;
            Q1=makeQuery(id+"F16.imprint","IMPRINT",FACE,{"disambiguationData":[TD([[makeQuery(id+"F16.imprint","IMPRINT",EDGE,{"derivedFrom":makeQuery(id+"F1.opExtrude","CAP_EDGE",EDGE,{"disambiguationData":[OSD([sQuery(id+"F0.wireOp",EDGE,"E1.left")])],"isStart":true})}),-1.0]])]});
            var Q2;
            Q2=makeQuery(id+"F16.imprint","IMPRINT",FACE,{"disambiguationData":[TD([[makeQuery(id+"F16.imprint","IMPRINT",EDGE,{"derivedFrom":sQuery(id+"F16.wireOp",EDGE,"E80")}),-1.0]])]});
            var Q3;
            Q3=makeQuery(id+"F2.opExtrude","CAP_FACE",FACE,{"disambiguationData":[OSD([sQuery(id+"F0.wireOp",EDGE,"E12"),sQuery(id+"F0.wireOp",EDGE,"E13"),sQuery(id+"F0.wireOp",EDGE,"E14"),sQuery(id+"F0.wireOp",EDGE,"E15"),sQuery(id+"F0.wireOp",EDGE,"E17.filletArc"),sQuery(id+"F0.wireOp",EDGE,"E18.filletArc"),sQuery(id+"F0.wireOp",EDGE,"E19.filletArc"),sQuery(id+"F0.wireOp",EDGE,"E20.filletArc"),sQuery(id+"F0.wireOp",EDGE,"E25.0"),sQuery(id+"F0.wireOp",EDGE,"E25.1"),sQuery(id+"F0.wireOp",EDGE,"E25.2"),sQuery(id+"F0.wireOp",EDGE,"E25.3"),sQuery(id+"F0.wireOp",EDGE,"E25.4"),sQuery(id+"F0.wireOp",EDGE,"E25.5"),sQuery(id+"F0.wireOp",EDGE,"E25.6"),sQuery(id+"F0.wireOp",EDGE,"E25.7")])],"isStart":false});
            extrude(context, id + "F17", {"entities" : qUnion([Q0, Q1, Q2]), "operationType" : NewBodyOperationType.ADD, "endBound" : BoundingType.UP_TO_SURFACE, "endBoundEntityFace" : qUnion([Q3]), "depth" : 25 * mm});
        }
    });
